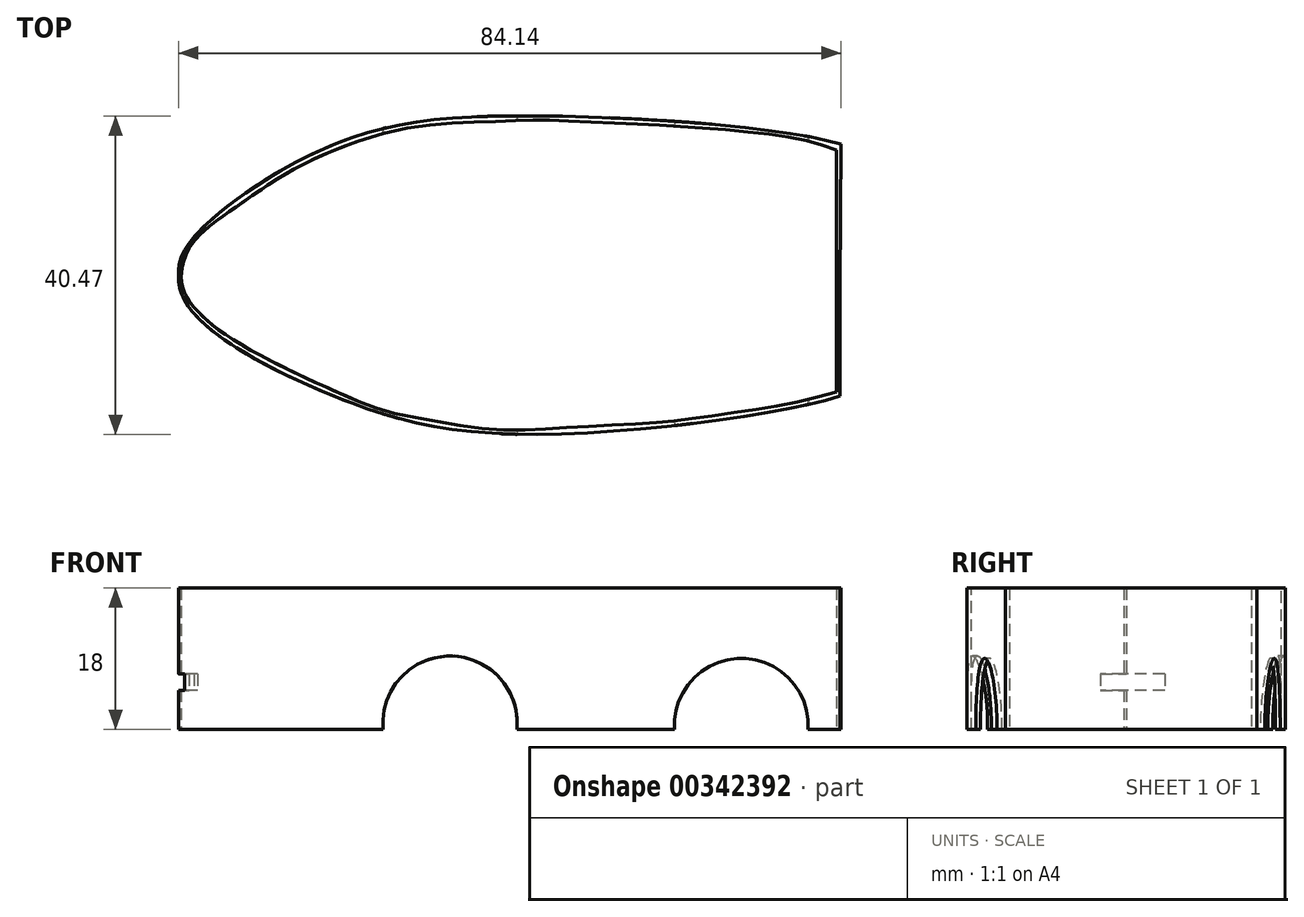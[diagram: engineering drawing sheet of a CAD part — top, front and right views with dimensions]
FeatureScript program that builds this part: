
annotation { "Feature Type Name" : "Feature", "Feature Type Description" : "" }
export const myFeature = defineFeature(function(context is Context, id is Id, definition is map)
    precondition{}
    {
        {
            var Q0;
            Q0=qCreatedBy(makeId("Top.planeOp"),FACE);
            var sketch = newSketch(context, id + "F0", { "sketchPlane" : qUnion([Q0])});
            skFitSpline(sketch, "E0", {"points": [v(38.67, 18.02) * mm, v(-1.71, 21.63) * mm, v(-25.73, 18.02) * mm, v(-42.02, 7.78) * mm, v(-45.45, 1.4) * mm], "startDerivative": vector(-64.35, 20.1) * mm, "endDerivative": vector(4.54, -45.94) * mm});
            skLineSegment(sketch, "E1", {"start": v(38.67, 18.02) * mm, "end": v(38.55, 3.02) * mm});
            skLineSegment(sketch, "E2.left", {"start": v(38.67, 18.02) * mm, "end": v(38.55, 0.17) * mm});
            skFitSpline(sketch, "E3.MirrorCS", {"points": [v(38.55, -13.98) * mm, v(-1.71, -18.83) * mm, v(-25.73, -13.98) * mm, v(-42.02, -4.98) * mm, v(-45.45, 1.4) * mm], "startDerivative": vector(-64.35, -20.1) * mm, "endDerivative": vector(4.54, 45.94) * mm});
            skLineSegment(sketch, "E4.MirrorCS", {"start": v(38.55, -13.98) * mm, "end": v(38.55, 0.17) * mm});
            skLineSegment(sketch, "E5", {"start": v(-23.45, 18.88) * mm, "end": v(-23.45, -14.88) * mm});
            skSolve(sketch);
        }
        {
            var Q0;
            Q0=qSketchRegion(id+"F0",true);
            extrude(context, id + "F1", {"entities" : qUnion([Q0]), "depth" : 18 * mm});
        }
        {
            var Q0;
            Q0=qCreatedBy(makeId("Front.planeOp"),FACE);
            cPlane(context, id + "F2", {"entities" : qUnion([Q0]), "cplaneType" : CPlaneType.OFFSET, "offset" : 18.8 * mm, "width" : 150 * mm, "height" : 150 * mm});
        }
        {
            var Q0;
            Q0=qCreatedBy(id+"F2.planeOp",FACE);
            var sketch = newSketch(context, id + "F3", { "sketchPlane" : qUnion([Q0])});
            skLineSegment(sketch, "E6.bottom", {"start": v(-19.5, 0) * mm, "end": v(-2.5, 0) * mm});
            skLineSegment(sketch, "E7.bottom", {"start": v(34.5, 0) * mm, "end": v(17.5, 0) * mm});
            skLineSegment(sketch, "E8", {"start": v(17.5, 0) * mm, "end": v(34.5, 0) * mm});
            skArc(sketch, "E9", {"start": v(-2.5, 0) * mm, "mid": v(-11, 9.35) * mm, "end": v(-19.5, 0) * mm});
            skArc(sketch, "E10", {"start": v(34.5, 0) * mm, "mid": v(26, 9.05) * mm, "end": v(17.5, 0) * mm});
            skSolve(sketch);
        }
        {
            var Q0;
            Q0 = qSketchRegion(id + "F3", true);
            extrude(context, id + "F4", {"entities" : qUnion([Q0]), "operationType" : NewBodyOperationType.REMOVE, "oppositeDirection" : true, "depth" : 54.4 * mm, "hasSecondDirection" : true, "secondDirectionOppositeDirection" : false, "secondDirectionDepth" : 100 * mm});
        }
        {
            var Q0;
            Q0=qCreatedBy(makeId("Top.planeOp"),FACE);
            var sketch = newSketch(context, id + "F5", { "sketchPlane" : qUnion([Q0])});
            skFitSpline(sketch, "E11", {"points": [v(-45.14, 1.1) * mm, v(-44.74, -0.85) * mm, v(-42.38, -3.89) * mm, v(-39.08, -6.44) * mm, v(-33.15, -9.81) * mm, v(-24.46, -13.85) * mm, v(-19.35, -15.8) * mm, v(-12.88, -17.15) * mm, v(-5.8, -18.16) * mm, v(0.66, -18.16) * mm, v(7.33, -17.76) * mm, v(14.8, -17.36) * mm, v(19.38, -16.88) * mm, v(25.85, -15.94) * mm, v(32.45, -14.86) * mm, v(38.1, -13.45) * mm], "startDerivative": vector(3.49, -48.19) * mm, "endDerivative": vector(83.35, 22.8) * mm});
            skLineSegment(sketch, "E12", {"start": v(38.1, -13.45) * mm, "end": v(38.1, 17.26) * mm});
            skFitSpline(sketch, "E13", {"points": [v(38.1, 17.26) * mm, v(34.07, 18.54) * mm, v(27.8, 19.49) * mm, v(19.38, 20.23) * mm, v(11.57, 20.63) * mm, v(2.95, 21.04) * mm, v(-1.9, 21.04) * mm, v(-9.04, 20.77) * mm, v(-17.46, 19.9) * mm, v(-27.43, 16.52) * mm, v(-33.56, 13.22) * mm, v(-39.15, 9.38) * mm, v(-44.2, 4.74) * mm, v(-45.14, 1.1) * mm, v(-45.1, 0.47) * mm], "startDerivative": vector(-64.93, 23.55) * mm, "endDerivative": vector(3.23, -21.49) * mm});
            skLineSegment(sketch, "E14", {"start": v(-22.64, 18.42) * mm, "end": v(-22.64, -14.64) * mm});
            skSolve(sketch);
        }
        {
            var Q0;
            Q0 = qSketchRegion(id + "F5", true);
            extrude(context, id + "F6", {"entities" : qUnion([Q0]), "operationType" : NewBodyOperationType.REMOVE, "depth" : 30.8 * mm});
        }
        {
            var Q0;
            Q0=qCreatedBy(makeId("Right.planeOp"),FACE);
            cPlane(context, id + "F7", {"entities" : qUnion([Q0]), "cplaneType" : CPlaneType.OFFSET, "offset" : 93.1 * mm, "width" : 150 * mm, "height" : 150 * mm});
        }
        {
            var Q0;
            Q0=qCreatedBy(id+"F7.planeOp",FACE);
            cPlane(context, id + "F8", {"entities" : qUnion([Q0]), "cplaneType" : CPlaneType.OFFSET, "offset" : 165.1 * mm, "oppositeDirection" : true, "width" : 150 * mm, "height" : 150 * mm});
        }
        {
            var Q0;
            Q0=qCreatedBy(id+"F8.planeOp",FACE);
            var sketch = newSketch(context, id + "F9", { "sketchPlane" : qUnion([Q0])});
            skLineSegment(sketch, "E15.bottom", {"start": v(6.27, 7.07) * mm, "end": v(-1.88, 7.07) * mm});
            skLineSegment(sketch, "E15.top", {"start": v(6.27, 5) * mm, "end": v(-1.88, 5) * mm});
            skLineSegment(sketch, "E15.left", {"start": v(6.27, 7.07) * mm, "end": v(6.27, 5) * mm});
            skLineSegment(sketch, "E15.right", {"start": v(-1.88, 7.07) * mm, "end": v(-1.88, 5) * mm});
            skSolve(sketch);
        }
        {
            var Q0;
            Q0 = qSketchRegion(id + "F9", true);
            extrude(context, id + "F10", {"entities" : qUnion([Q0]), "operationType" : NewBodyOperationType.REMOVE, "depth" : 75 * mm});
        }
    });
